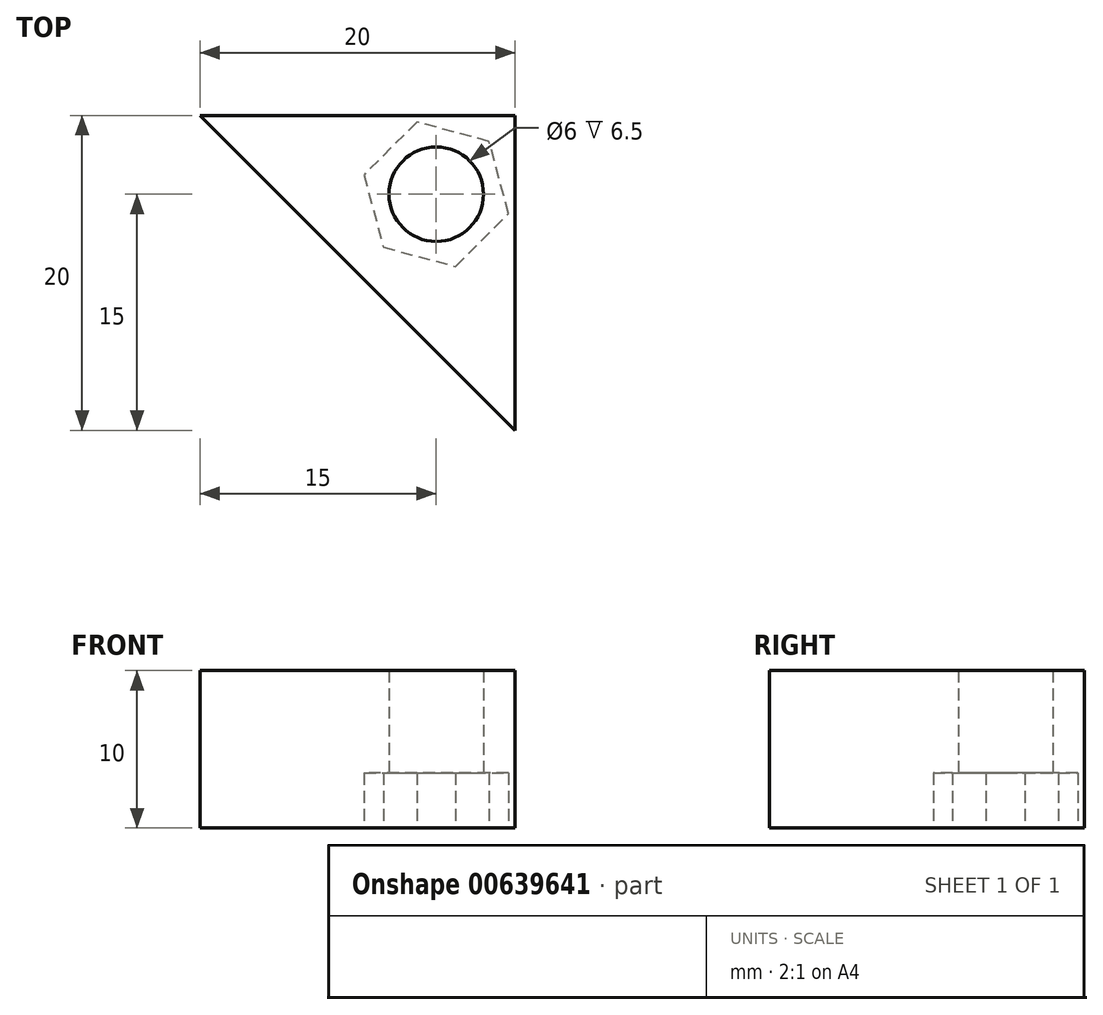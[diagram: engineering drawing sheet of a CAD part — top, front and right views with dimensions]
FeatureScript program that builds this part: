
annotation { "Feature Type Name" : "Feature", "Feature Type Description" : "" }
export const myFeature = defineFeature(function(context is Context, id is Id, definition is map)
    precondition{}
    {
        {
            var Q0;
            Q0=qCreatedBy(makeId("Top.planeOp"),FACE);
            var sketch = newSketch(context, id + "F0", { "sketchPlane" : qUnion([Q0])});
            skLineSegment(sketch, "E0", {"start": v(0, 0) * mm, "end": v(0, -20) * mm});
            skLineSegment(sketch, "E1", {"start": v(0, 0) * mm, "end": v(-20, 0) * mm});
            skLineSegment(sketch, "E2", {"start": v(-20, 0) * mm, "end": v(0, -20) * mm});
            skSolve(sketch);
        }
        {
            var Q0;
            Q0=makeQuery(id+"F0.imprint","IMPRINT",FACE,{"disambiguationData":[TD([[makeQuery(id+"F0.imprint","IMPRINT",EDGE,{"derivedFrom":sQuery(id+"F0.wireOp",EDGE,"E0")}),-1.0]])]});
            extrude(context, id + "F1", {"entities" : qUnion([Q0]), "depth" : 7.5 * mm, "offsetDistance" : 25 * mm});
        }
        {
            var Q0;
            Q0=makeQuery(id+"F1.opExtrude","CAP_FACE",FACE,{"disambiguationData":[OSD([sQuery(id+"F0.wireOp",EDGE,"E0"),sQuery(id+"F0.wireOp",EDGE,"E1"),sQuery(id+"F0.wireOp",EDGE,"E2")])],"isStart":true});
            extrude(context, id + "F2", {"entities" : qUnion([Q0]), "operationType" : NewBodyOperationType.ADD, "depth" : 2.5 * mm, "offsetDistance" : 25 * mm});
        }
        {
            var Q0;
            Q0=makeQuery(id+"F2.opExtrude","CAP_FACE",FACE,{"disambiguationData":[OSD([sQuery(id+"F0.wireOp",EDGE,"E0"),sQuery(id+"F0.wireOp",EDGE,"E1"),sQuery(id+"F0.wireOp",EDGE,"E2")])],"isStart":false});
            var sketch = newSketch(context, id + "F3", { "sketchPlane" : qUnion([Q0])});
            skLineSegment(sketch, "E3", {"start": v(-10, 10) * mm, "end": v(-5, 5) * mm});
            skCircle(sketch, "E4", {"center": v(-5, 5) * mm, "radius": 3 * mm});
            skLineSegment(sketch, "E5.0", {"start": v(-8.36, 8.36) * mm, "end": v(-3.77, 9.59) * mm});
            skLineSegment(sketch, "E5.1", {"start": v(-3.77, 9.59) * mm, "end": v(-0.41, 6.23) * mm});
            skLineSegment(sketch, "E5.2", {"start": v(-0.41, 6.23) * mm, "end": v(-1.64, 1.64) * mm});
            skLineSegment(sketch, "E5.3", {"start": v(-1.64, 1.64) * mm, "end": v(-6.23, 0.41) * mm});
            skLineSegment(sketch, "E5.4", {"start": v(-6.23, 0.41) * mm, "end": v(-9.59, 3.77) * mm});
            skLineSegment(sketch, "E5.5", {"start": v(-9.59, 3.77) * mm, "end": v(-8.36, 8.36) * mm});
            skSolve(sketch);
        }
        {
            var Q0;
            Q0=makeQuery(id+"F3.imprint","IMPRINT",FACE,{"disambiguationData":[TD([[makeQuery(id+"F3.imprint","IMPRINT",EDGE,{"derivedFrom":sQuery(id+"F3.wireOp",EDGE,"E4")}),1.0]])]});
            extrude(context, id + "F4", {"entities" : qUnion([Q0]), "operationType" : NewBodyOperationType.REMOVE, "oppositeDirection" : true, "depth" : 25 * mm, "offsetDistance" : 25 * mm});
        }
        {
            var Q0;
            Q0=makeQuery(id+"F3.imprint","IMPRINT",FACE,{"disambiguationData":[TD([[makeQuery(id+"F3.imprint","IMPRINT",EDGE,{"derivedFrom":sQuery(id+"F3.wireOp",EDGE,"E4")}),-1.0]])]});
            extrude(context, id + "F5", {"entities" : qUnion([Q0]), "operationType" : NewBodyOperationType.REMOVE, "oppositeDirection" : true, "depth" : 3.5 * mm, "offsetDistance" : 25 * mm});
        }
    });
